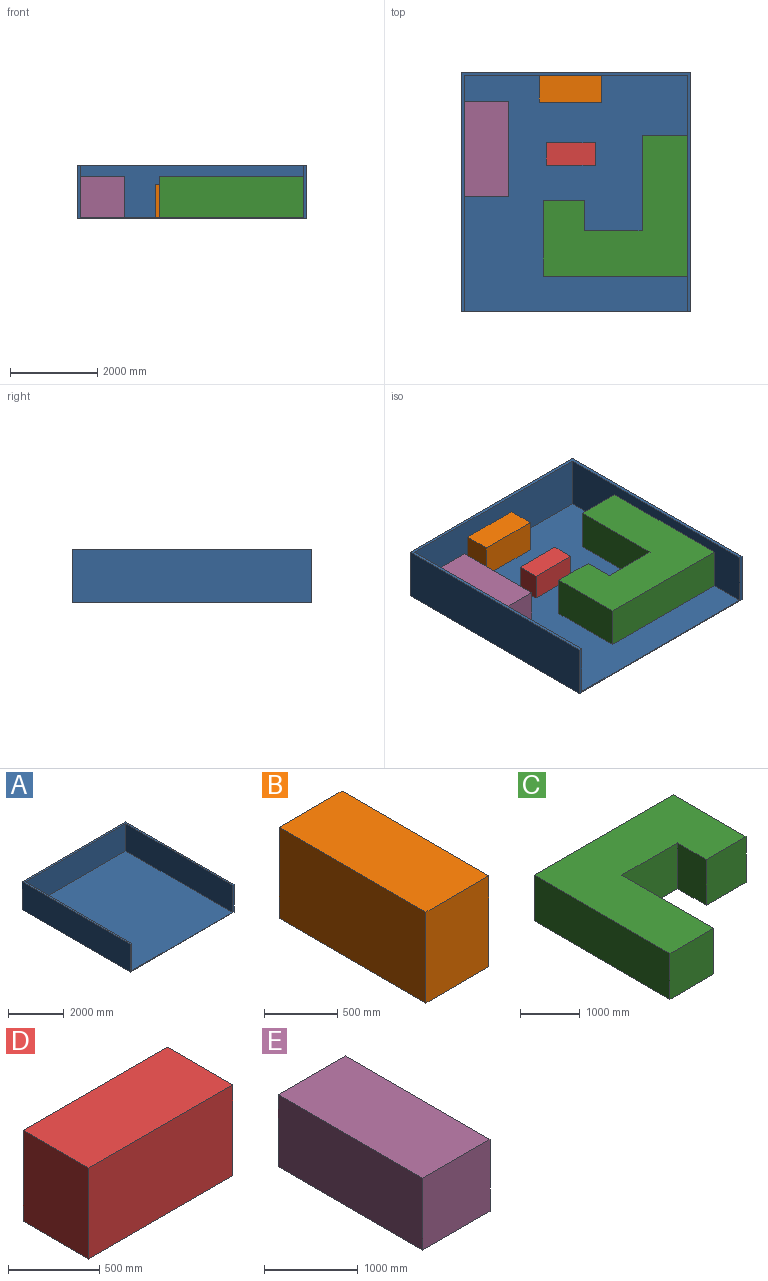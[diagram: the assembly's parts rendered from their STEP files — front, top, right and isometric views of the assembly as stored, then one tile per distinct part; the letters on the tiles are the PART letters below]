
ASSEMBLY  parts=5 mates=7
PART A: 10 faces, bbox 5257.8x5486.4x1219.2 mm
  f0: plane 5105.4x1193.8mm, normal (0,-1,0), area 6094826.5mm2, adj f1,f6,f7,f9
  f1: plane 5410.2x1193.8mm, normal (-1,0,0), area 6458696.8mm2, adj f0,f5,f7,f9
  f2: plane 5486.4x1219.2mm, normal (1,0,0), area 6689018.9mm2, adj f3,f5,f7,f8
  f3: plane 5257.8x1219.2mm, normal (0,1,0), area 6410309.8mm2, adj f2,f4,f7,f8
  f4: plane 5486.4x1219.2mm, normal (-1,0,0), area 6689018.9mm2, adj f3,f5,f7,f8
  f5: plane 5257.8x1219.2mm, normal (0,-1,0), area 315483.2mm2, adj f1,f2,f4,f6,f7,f8,f9
  f6: plane 5410.2x1193.8mm, normal (1,0,0), area 6458696.8mm2, adj f0,f5,f7,f9
  f7: plane 5486.4x5257.8mm, normal (0,0,1), area 1225158.8mm2, adj f0,f1,f2,f3,f4,f5,f6
  f8: plane 5486.4x5257.8mm, normal (0,0,-1), area 28846393.9mm2, adj f2,f3,f4,f5
  f9: plane 5410.2x5105.4mm, normal (0,0,1), area 27621235.1mm2, adj f0,f1,f5,f6
PART B: 6 faces, bbox 609.6x1422.4x762 mm
  f0: plane 1422.4x762mm, normal (1,0,0), area 1083868.8mm2, adj f1,f3,f4,f5
  f1: plane 762x609.6mm, normal (0,1,0), area 464515.2mm2, adj f0,f2,f4,f5
  f2: plane 1422.4x762mm, normal (-1,0,0), area 1083868.8mm2, adj f1,f3,f4,f5
  f3: plane 762x609.6mm, normal (0,-1,0), area 464515.2mm2, adj f0,f2,f4,f5
  f4: plane 1422.4x609.6mm, normal (0,0,1), area 867095mm2, adj f0,f1,f2,f3
  f5: plane 1422.4x609.6mm, normal (0,0,-1), area 867095mm2, adj f0,f1,f2,f3
PART C: 10 faces, bbox 3302x3225.8x939.8 mm
  f0: plane 3225.8x939.8mm, normal (-1,0,0), area 3031606.8mm2, adj f1,f7,f8,f9
  f1: plane 1041.4x939.8mm, normal (0,-1,0), area 978707.7mm2, adj f0,f2,f8,f9
  f2: plane 2184.4x939.8mm, normal (1,0,0), area 2052899.1mm2, adj f1,f3,f8,f9
  f3: plane 1320.8x939.8mm, normal (0,-1,0), area 1241287.8mm2, adj f2,f4,f8,f9
  f4: plane 939.8x685.8mm, normal (-1,0,0), area 644514.8mm2, adj f3,f5,f8,f9
  f5: plane 939.8x939.8mm, normal (0,-1,0), area 883224mm2, adj f4,f6,f8,f9
  f6: plane 1727.2x939.8mm, normal (1,0,0), area 1623222.6mm2, adj f5,f7,f8,f9
  f7: plane 3302x939.8mm, normal (0,1,0), area 3103219.6mm2, adj f0,f6,f8,f9
  f8: plane 3302x3225.8mm, normal (0,0,1), area 6358051.8mm2, adj f0,f1,f2,f3,f4,f5,f6,f7
  f9: plane 3302x3225.8mm, normal (0,0,-1), area 6358051.8mm2, adj f0,f1,f2,f3,f4,f5,f6,f7
PART D: 6 faces, bbox 1117.6x508x609.6 mm
  f0: plane 609.6x508mm, normal (1,0,0), area 309676.8mm2, adj f1,f3,f4,f5
  f1: plane 1117.6x609.6mm, normal (0,1,0), area 681289mm2, adj f0,f2,f4,f5
  f2: plane 609.6x508mm, normal (-1,0,0), area 309676.8mm2, adj f1,f3,f4,f5
  f3: plane 1117.6x609.6mm, normal (0,-1,0), area 681289mm2, adj f0,f2,f4,f5
  f4: plane 1117.6x508mm, normal (0,0,1), area 567740.8mm2, adj f0,f1,f2,f3
  f5: plane 1117.6x508mm, normal (0,0,-1), area 567740.8mm2, adj f0,f1,f2,f3
PART E: 6 faces, bbox 1016x2184.4x939.8 mm
  f0: plane 2184.4x939.8mm, normal (1,0,0), area 2052899.1mm2, adj f1,f3,f4,f5
  f1: plane 1016x939.8mm, normal (0,1,0), area 954836.8mm2, adj f0,f2,f4,f5
  f2: plane 2184.4x939.8mm, normal (-1,0,0), area 2052899.1mm2, adj f1,f3,f4,f5
  f3: plane 1016x939.8mm, normal (0,-1,0), area 954836.8mm2, adj f0,f2,f4,f5
  f4: plane 2184.4x1016mm, normal (0,0,1), area 2219350.4mm2, adj f0,f1,f2,f3
  f5: plane 2184.4x1016mm, normal (0,0,-1), area 2219350.4mm2, adj f0,f1,f2,f3
PLACE A t=(-27.94,142.53,1110.1)mm fixed
PLACE B rot(axis=(0,0,1),90deg) t=(-159.66,2542.83,1135.5)mm
PLACE C rot(axis=(0,0,1),180deg) t=(822.96,211.06,1135.5)mm
PLACE D t=(-146.86,1051.11,1135.5)mm
PLACE E t=(-2072.64,1163,1135.5)mm
MATE planar A.f1 <-> C.f0  axis (-1,0,0) through (2524.76,142.53,1732.4)mm
MATE planar A.f9 <-> C.f9  axis (0,0,1) through (-27.94,142.53,1135.5)mm
MATE planar A.f0 <-> B.f0  axis (0,-1,0) through (-27.94,2847.63,1732.4)mm
MATE planar A.f6 <-> E.f2  axis (1,0,0) through (-2580.64,142.53,1732.4)mm
MATE planar A.f9 <-> B.f5  axis (0,0,1) through (-27.94,142.53,1135.5)mm
MATE planar E.f5 <-> A.f9  axis (0,0,-1) through (-2072.64,1163,1135.5)mm
MATE planar D.f5 <-> A.f9  axis (0,0,-1) through (-705.66,797.11,1135.5)mm
